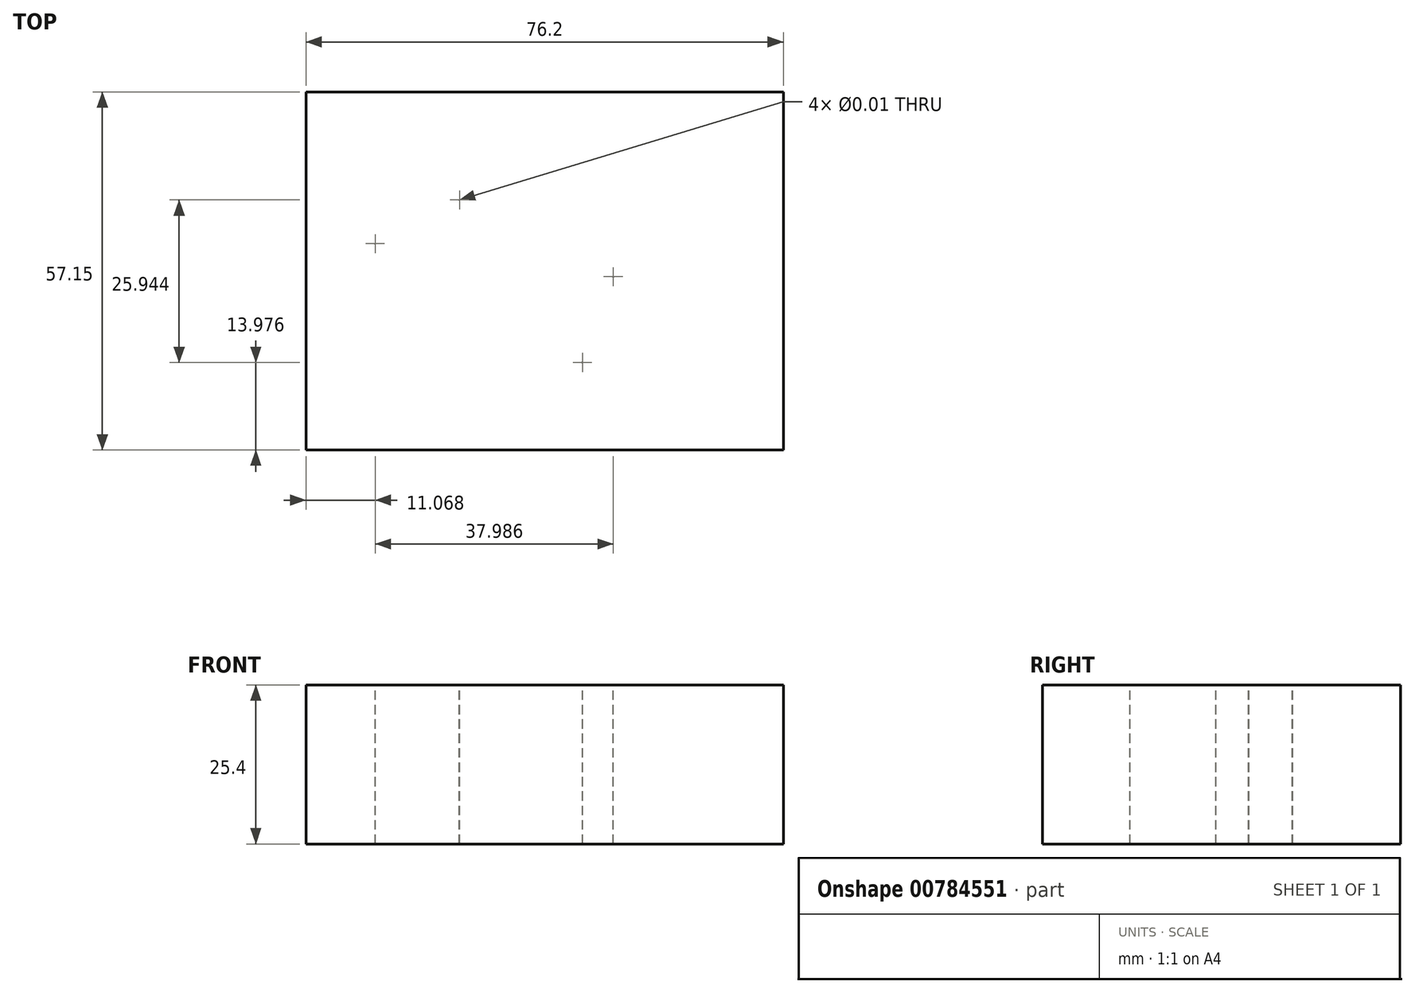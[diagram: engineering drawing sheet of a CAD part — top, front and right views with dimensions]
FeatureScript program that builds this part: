
annotation { "Feature Type Name" : "Feature", "Feature Type Description" : "" }
export const myFeature = defineFeature(function(context is Context, id is Id, definition is map)
    precondition{}
    {
        {
            var Q0;
            Q0=qCreatedBy(makeId("Top.planeOp"),FACE);
            var sketch = newSketch(context, id + "F0", { "sketchPlane" : qUnion([Q0])});
            skLineSegment(sketch, "E0.bottom", {"start": v(0, 0) * mm, "end": v(76.2, 0) * mm});
            skLineSegment(sketch, "E0.top", {"start": v(0, -57.15) * mm, "end": v(76.2, -57.15) * mm});
            skLineSegment(sketch, "E0.left", {"start": v(0, 0) * mm, "end": v(0, -57.15) * mm});
            skLineSegment(sketch, "E0.right", {"start": v(76.2, 0) * mm, "end": v(76.2, -57.15) * mm});
            skSolve(sketch);
        }
        {
            var Q0;
            Q0=makeQuery(id+"F0.imprint","IMPRINT",FACE,{"disambiguationData":[TD([[makeQuery(id+"F0.imprint","IMPRINT",EDGE,{"derivedFrom":sQuery(id+"F0.wireOp",EDGE,"E0.bottom")}),-1.0]])]});
            extrude(context, id + "F1", {"entities" : qUnion([Q0]), "depth" : 25.4 * mm, "offsetDistance" : 25.4 * mm});
        }
        {
            var Q0;
            Q0=makeQuery(id+"F1.opExtrude","CAP_FACE",FACE,{"disambiguationData":[OSD([sQuery(id+"F0.wireOp",EDGE,"E0.bottom"),sQuery(id+"F0.wireOp",EDGE,"E0.top"),sQuery(id+"F0.wireOp",EDGE,"E0.left"),sQuery(id+"F0.wireOp",EDGE,"E0.right")])],"isStart":false});
            var sketch = newSketch(context, id + "F2", { "sketchPlane" : qUnion([Q0])});
            skPoint(sketch, "E1", {"position": v(49.05, -29.47) * mm});
            skPoint(sketch, "E2", {"position": v(24.51, -17.23) * mm});
            skPoint(sketch, "E3", {"position": v(11.07, -24.22) * mm});
            skPoint(sketch, "E4", {"position": v(44.15, -43.17) * mm});
            skSolve(sketch);
        }
        {
            var Q0;
            Q0=sQuery(id+"F2.wireOp",VERTEX,"E1");
            var Q1;
            Q1=sQuery(id+"F2.wireOp",VERTEX,"E2");
            var Q2;
            Q2=sQuery(id+"F2.wireOp",VERTEX,"E3");
            var Q3;
            Q3=sQuery(id+"F2.wireOp",VERTEX,"E4");
            var Q4;
            Q4=makeQuery(id+"F1.opExtrude","SWEPT_BODY",BODY,{"disambiguationData":[OSD([sQuery(id+"F0.wireOp",EDGE,"E0.bottom"),sQuery(id+"F0.wireOp",EDGE,"E0.top"),sQuery(id+"F0.wireOp",EDGE,"E0.left"),sQuery(id+"F0.wireOp",EDGE,"E0.right")])]});
            hole(context, id + "F3", {"style" : HoleStyle.SIMPLE, "endStyle" : HoleEndStyle.THROUGH, "standardTappedOrClearance" : lookupTablePath({ "standard" : "ANSI", "size" : "3/8 (0.38)", "type" : "Drilled" }), "standardBlindInLast" : lookupTablePath({ "standard" : "ANSI", "size" : "3/8", "type" : "Drilled" }), "holeDiameter" : 3 / 203.2 * mm, "majorDiameter" : 6.35 * mm, "isTappedThrough" : true, "tappedDepth" : 12.7 * mm, "tapClearance" : 3, "locations" : qUnion([Q0, Q1, Q2, Q3]), "scope" : qUnion([Q4])});
        }
    });
